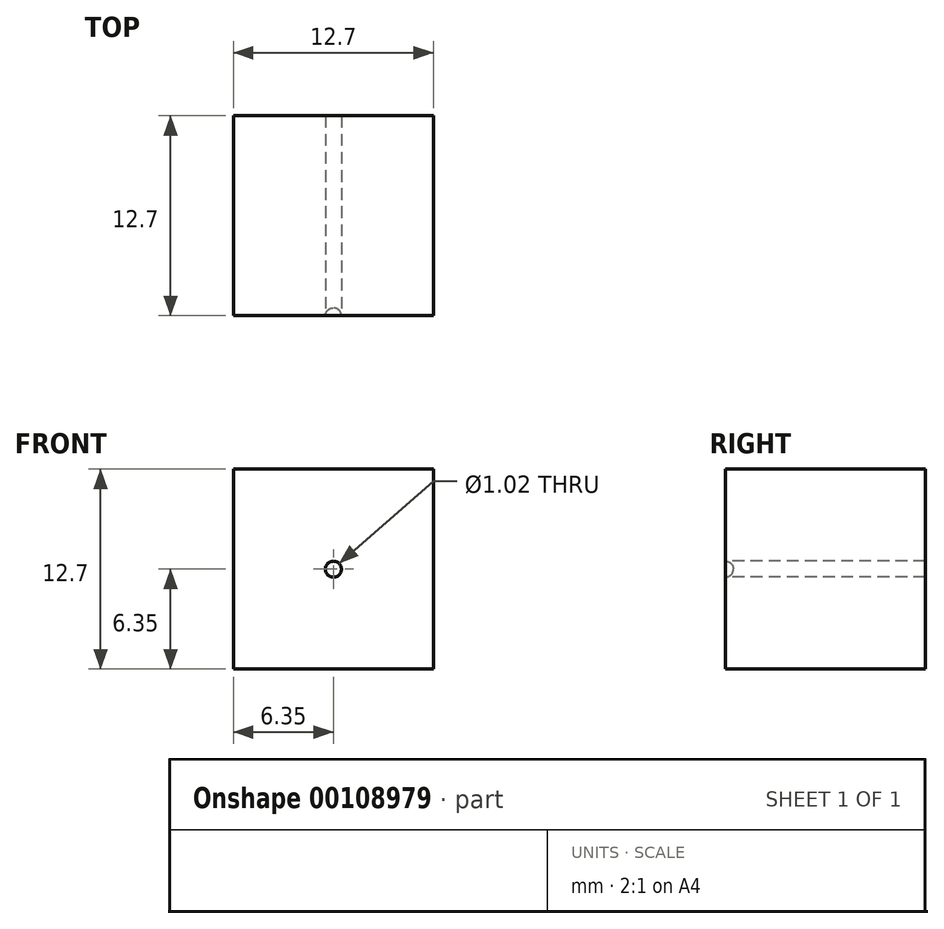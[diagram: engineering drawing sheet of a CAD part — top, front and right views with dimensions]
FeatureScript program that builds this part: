
annotation { "Feature Type Name" : "Feature", "Feature Type Description" : "" }
export const myFeature = defineFeature(function(context is Context, id is Id, definition is map)
    precondition{}
    {
        {
            var Q0;
            Q0=qCreatedBy(makeId("Right.planeOp"),FACE);
            var sketch = newSketch(context, id + "F0", { "sketchPlane" : qUnion([Q0])});
            skLineSegment(sketch, "E0", {"start": v(0, 0) * mm, "end": v(0, 0.5) * mm});
            skLineSegment(sketch, "E1", {"start": v(0, 0) * mm, "end": v(-0.5, 0) * mm});
            skArc(sketch, "E2", {"start": v(0, 0.5) * mm, "mid": v(-0.36, 0.36) * mm, "end": v(-0.5, 0) * mm});
            skSolve(sketch);
        }
        {
            var Q0;
            Q0=makeQuery(id+"F0.imprint","IMPRINT",FACE,{"disambiguationData":[TD([[makeQuery(id+"F0.imprint","IMPRINT",EDGE,{"derivedFrom":sQuery(id+"F0.wireOp",EDGE,"E0")}),1.0]])]});
            var Q1;
            Q1=sQuery(id+"F0.wireOp",EDGE,"E1");
            revolve(context, id + "F1", {"entities" : qUnion([Q0]), "axis" : qUnion([Q1]), "revolveType" : RevolveType.FULL});
        }
        {
            var Q0;
            Q0=makeQuery(id+"F1.opRevolve","SWEPT_FACE",FACE,{"disambiguationData":[OSD([sQuery(id+"F0.wireOp",EDGE,"E0")])]});
            var sketch = newSketch(context, id + "F2", { "sketchPlane" : qUnion([Q0])});
            skLineSegment(sketch, "E3.bottom", {"start": v(6.35, -6.35) * mm, "end": v(-6.35, -6.35) * mm});
            skLineSegment(sketch, "E3.top", {"start": v(6.35, 6.35) * mm, "end": v(-6.35, 6.35) * mm});
            skLineSegment(sketch, "E3.left", {"start": v(6.35, -6.35) * mm, "end": v(6.35, 6.35) * mm});
            skLineSegment(sketch, "E3.right", {"start": v(-6.35, -6.35) * mm, "end": v(-6.35, 6.35) * mm});
            skPoint(sketch, "E3.middle", {"position": v(0, 0) * mm});
            skSolve(sketch);
        }
        {
            var Q0;
            Q0=makeQuery(id+"F2.imprint","IMPRINT",FACE,{"disambiguationData":[TD([[makeQuery(id+"F2.imprint","IMPRINT",EDGE,{"derivedFrom":sQuery(id+"F2.wireOp",EDGE,"E3.bottom")}),-1.0]])]});
            extrude(context, id + "F3", {"entities" : qUnion([Q0]), "depth" : 12.7 * mm});
        }
    });
